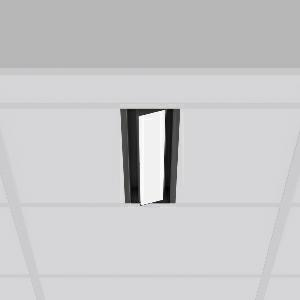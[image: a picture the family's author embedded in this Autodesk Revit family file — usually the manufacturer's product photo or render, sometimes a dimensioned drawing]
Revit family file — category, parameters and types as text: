
# Revit family: tx-move_901731_003_2_76_f08b
name_source: partatom
category: Lighting Fixtures
units: mm (PartAtom-declared; Revit-internal decimal feet)

## family parameters
Cut with Voids When Loaded = No
Host = Face
Light Source = No
Part Type = Normal
Room Calculation Point = No
Round Connector Dimension = Use Diameter
Shared = No

## types (1)
- MultiLumen 1 (1 x LED Modul 927, 1700 lm, 2700)
    Apparent Load = 16 VA
    Approval mark = CE
    CIE Flux Codes = 47 79 96 100 100
    Color Rendering = 92
    Color Temperature = 2700
    Default Elevation = 1800 mm
    Description = Series: TX-MOVE
Einlege/Einbau-Flächenstrahler. Housing: sheet steel, powder-coated. Swivel range: 90°. High-efficiency LED units with flush-mounted opal diffuser made of non-yellowing PMMA. Symmetrical wide beam light emission. Suitable for laying in grid ceiling module 625. Connected converter included in separate gearbox.Suitable for through-wiring.MultiLumen: Luminous flux adjustable in 3 steps. Accessories: Mounting frame for installation in suspended ceilings. Environmentally friendly and resource-saving due to replaceable and recyclable components. 
Colour: deep black, matt (RAL 9005)
Length: 622 mm
Width: 116 mm
Height: 39 mm
Cut-out length: 602 mm
Cut-out width: 98 mm
Recess height: 100 mm
Lamp: LED
Socket: without socket
Colour temperature: 2700K
Colour rendering index (CRI): 90
System power: 16 W
Rated luminous flux: 1700 lm
Luminous efficiency: 106 lm/W
System power 2: 23 W
Rated luminous flux 2: 2350 lm
Luminous efficiency 2: 102 lm/W
System power 3: 31 W
Rated luminous flux 3: 3050 lm
Luminous efficiency 3: 98 lm/W
Control gear: Dimmable EVG, DALI
Protection class: I
Type of protection: IP 20
    Height = 0 mm  [stored 0 ft]
    Lamp = 1 x LED Modul 927
    Lamp Light Flux = 1700 lm
    Lamp count = 1
    Length = 622 mm
    Lifetime = 50000 h
    Luminous efficacy = 106 lm/W
    Manufacturer = RZB
    ModVariant = No
    Model = 901731.003.2.76
    Mounting Place = Ceiling, Wall
    Mounting Type = Recessed
    Number of Poles = 1
    OnlyDefault = Yes
    Power Factor = 1
    Product Name = TX-MOVE
    Product group = Recessed projectors
    ProductGroupID = 401
    Protection Class = Protection class I
    Protection Degree = IP 20
    RLX_Detail_Level = 1
    RLX_Emergency_Light_Flux = 0 lm
    RLX_Emergency_Type = 0
    RLX_Emergency_Type_DB = No
    RlxData = <blob elided: 26049 chars, md5=447f6241>
    Socket = socket
    Standby Power = 0 W
    System Light Flux = 1700 lm
    System Power = 16 W
    Type Comments = MultiLumen 1
    Type Image = 901731.003.jpg
    URL = http://relux.com
    VarID = multilumen_1
    Voltage = 230 V
    Voltage Range = 220-240 V
    Weight = 0.00 kg
    Width = 116 mm

note: [stored X ft] marks values corroborated as IEEE doubles in the binary element streams (Revit-internal decimal feet)

## geometry (parser evidence)
native form markers: Blend x4, Sweep x11
no freeform markers — native parametric forms only
